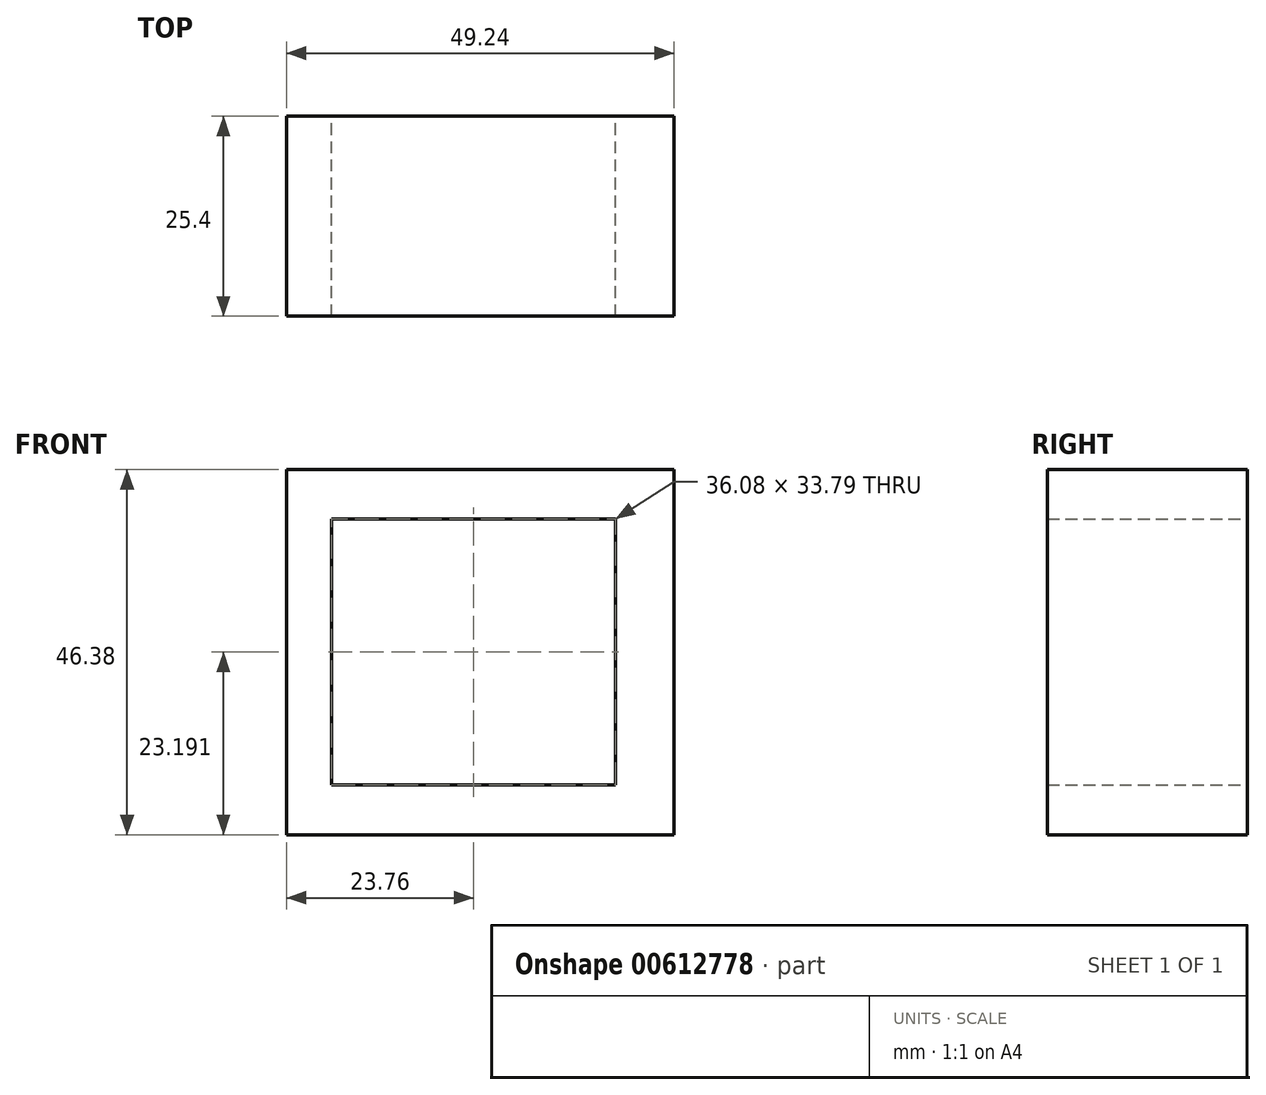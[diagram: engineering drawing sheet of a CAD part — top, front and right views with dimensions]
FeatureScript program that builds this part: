
annotation { "Feature Type Name" : "Feature", "Feature Type Description" : "" }
export const myFeature = defineFeature(function(context is Context, id is Id, definition is map)
    precondition{}
    {
        {
            var Q0;
            Q0=qCreatedBy(makeId("Front.planeOp"),FACE);
            var sketch = newSketch(context, id + "F0", { "sketchPlane" : qUnion([Q0])});
            skLineSegment(sketch, "E0.bottom", {"start": v(18.04, 13.74) * mm, "end": v(-18.04, 13.74) * mm});
            skLineSegment(sketch, "E0.top", {"start": v(18.04, -20.04) * mm, "end": v(-18.04, -20.04) * mm});
            skLineSegment(sketch, "E0.left", {"start": v(18.04, 13.74) * mm, "end": v(18.04, -20.04) * mm});
            skLineSegment(sketch, "E0.right", {"start": v(-18.04, 13.74) * mm, "end": v(-18.04, -20.04) * mm});
            skLineSegment(sketch, "E1.bottom", {"start": v(25.48, 20.04) * mm, "end": v(-23.76, 20.04) * mm});
            skLineSegment(sketch, "E1.top", {"start": v(25.48, -26.34) * mm, "end": v(-23.76, -26.34) * mm});
            skLineSegment(sketch, "E1.left", {"start": v(25.48, 20.04) * mm, "end": v(25.48, -26.34) * mm});
            skLineSegment(sketch, "E1.right", {"start": v(-23.76, 20.04) * mm, "end": v(-23.76, -26.34) * mm});
            skSolve(sketch);
        }
        {
            var Q0;
            Q0=makeQuery(id+"F0.imprint","IMPRINT",FACE,{"disambiguationData":[TD([[makeQuery(id+"F0.imprint","IMPRINT",EDGE,{"derivedFrom":sQuery(id+"F0.wireOp",EDGE,"E0.bottom")}),-1.0]])]});
            extrude(context, id + "F1", {"entities" : qUnion([Q0]), "depth" : 25.4 * mm, "offsetDistance" : 25.4 * mm});
        }
    });
